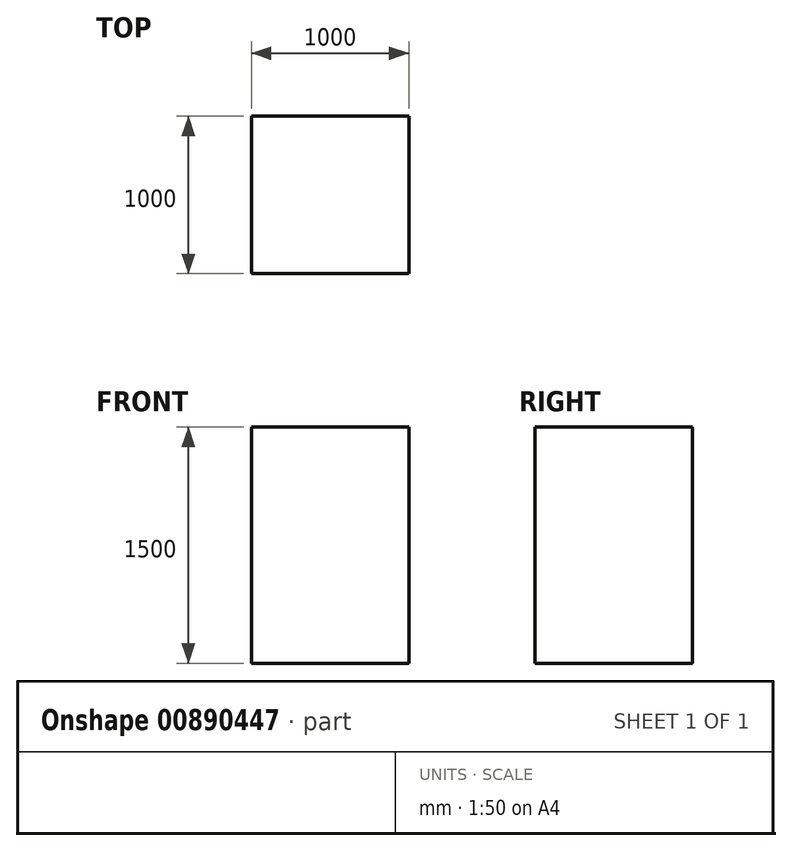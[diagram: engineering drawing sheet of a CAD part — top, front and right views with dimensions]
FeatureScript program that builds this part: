
annotation { "Feature Type Name" : "Feature", "Feature Type Description" : "" }
export const myFeature = defineFeature(function(context is Context, id is Id, definition is map)
    precondition{}
    {
        {
            var Q0;
            Q0=qCreatedBy(makeId("Top.planeOp"),FACE);
            var sketch = newSketch(context, id + "F0", { "sketchPlane" : qUnion([Q0])});
            skLineSegment(sketch, "E0.bottom", {"start": v(0, 0) * mm, "end": v(-1000, 0) * mm});
            skLineSegment(sketch, "E0.top", {"start": v(0, 1000) * mm, "end": v(-1000, 1000) * mm});
            skLineSegment(sketch, "E0.left", {"start": v(0, 0) * mm, "end": v(0, 1000) * mm});
            skLineSegment(sketch, "E0.right", {"start": v(-1000, 0) * mm, "end": v(-1000, 1000) * mm});
            skSolve(sketch);
        }
        {
            var Q0;
            Q0=makeQuery(id+"F0.imprint","IMPRINT",FACE,{"disambiguationData":[TD([[makeQuery(id+"F0.imprint","IMPRINT",EDGE,{"derivedFrom":sQuery(id+"F0.wireOp",EDGE,"E0.bottom")}),-1.0]])]});
            extrude(context, id + "F1", {"entities" : qUnion([Q0]), "depth" : 1500 * mm, "offsetDistance" : 25 * mm});
        }
    });
